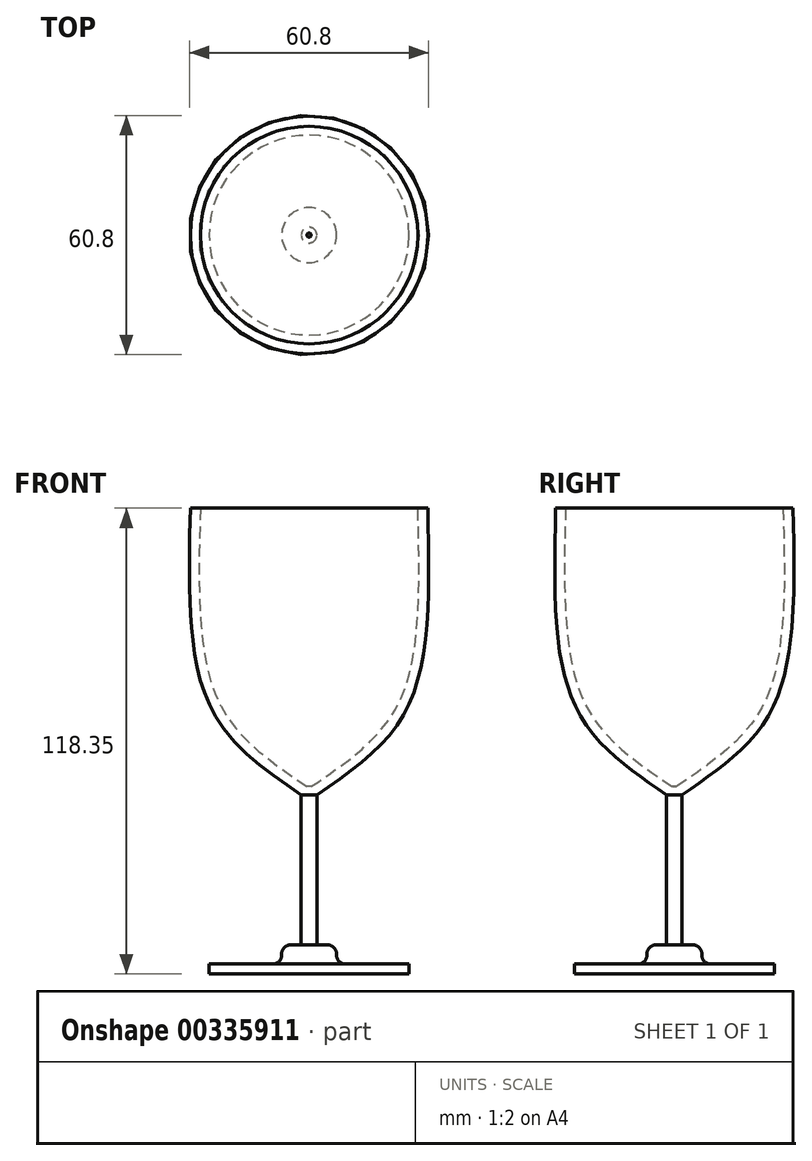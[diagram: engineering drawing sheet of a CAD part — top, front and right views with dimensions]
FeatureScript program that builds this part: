
annotation { "Feature Type Name" : "Feature", "Feature Type Description" : "" }
export const myFeature = defineFeature(function(context is Context, id is Id, definition is map)
    precondition{}
    {
        {
            var Q0;
            Q0=qCreatedBy(makeId("Front.planeOp"),FACE);
            var sketch = newSketch(context, id + "F0", { "sketchPlane" : qUnion([Q0])});
            skLineSegment(sketch, "E0", {"start": v(0, 0) * mm, "end": v(25.4, 0) * mm});
            skLineSegment(sketch, "E1", {"start": v(25.4, 0) * mm, "end": v(25.4, 2.54) * mm});
            skLineSegment(sketch, "E2", {"start": v(25.4, 2.54) * mm, "end": v(6.97, 2.54) * mm});
            skLineSegment(sketch, "E3", {"start": v(6.97, 2.54) * mm, "end": v(6.97, 7.42) * mm});
            skLineSegment(sketch, "E4", {"start": v(6.97, 7.42) * mm, "end": v(1.99, 7.42) * mm});
            skLineSegment(sketch, "E5", {"start": v(1.99, 7.42) * mm, "end": v(1.99, 45.52) * mm});
            skFitSpline(sketch, "E6", {"points": [v(1.99, 45.52) * mm, v(21.02, 61.4) * mm, v(29.15, 81.99) * mm, v(30.17, 118.35) * mm], "startDerivative": vector(67.56, 46.57) * mm, "endDerivative": vector(-2.25, 101.1) * mm});
            skFitSpline(sketch, "E7.0", {"points": [v(0.54, 47.61) * mm, v(1.95, 48.58) * mm, v(4.75, 50.51) * mm, v(8.8, 53.43) * mm, v(12.59, 56.41) * mm, v(15.43, 58.98) * mm, v(17.47, 61.1) * mm, v(18.87, 62.73) * mm, v(20.12, 64.4) * mm, v(21.64, 66.72) * mm, v(23.25, 69.8) * mm, v(24.77, 73.8) * mm, v(25.94, 78.2) * mm, v(26.8, 83) * mm, v(27.37, 88.23) * mm, v(27.82, 95.67) * mm, v(27.91, 105.68) * mm, v(27.73, 114.08) * mm, v(27.63, 118.3) * mm]});
            skLineSegment(sketch, "E8", {"start": v(30.17, 118.35) * mm, "end": v(27.63, 118.3) * mm});
            skLineSegment(sketch, "E9", {"start": v(0.54, 47.61) * mm, "end": v(0, 47.61) * mm});
            skLineSegment(sketch, "E10", {"start": v(0, 47.61) * mm, "end": v(0, 0) * mm});
            skSolve(sketch);
        }
        {
            var Q0;
            Q0=makeQuery(id+"F0.imprint","IMPRINT",FACE,{"disambiguationData":[TD([[makeQuery(id+"F0.imprint","IMPRINT",EDGE,{"derivedFrom":sQuery(id+"F0.wireOp",EDGE,"E0")}),1.0]])]});
            var Q1;
            Q1=sQuery(id+"F0.wireOp",EDGE,"E10");
            revolve(context, id + "F1", {"entities" : qUnion([Q0]), "axis" : qUnion([Q1]), "revolveType" : RevolveType.FULL});
        }
        {
            var Q0;
            Q0=makeQuery(id+"F1.opRevolve","SWEPT_EDGE",EDGE,{"disambiguationData":[OSD([sQuery(id+"F0.wireOp",EDGE,"E3"),sQuery(id+"F0.wireOp",EDGE,"E4")])]});
            var Q1;
            Q1=makeQuery(id+"F1.opRevolve","SWEPT_EDGE",EDGE,{"disambiguationData":[OSD([sQuery(id+"F0.wireOp",EDGE,"E2"),sQuery(id+"F0.wireOp",EDGE,"E3")])]});
            fillet(context, id + "F2", {"entities" : qUnion([Q0, Q1]), "radius" : 2.3 * mm, "tangentPropagation" : true, "allowEdgeOverflow" : false});
        }
    });
